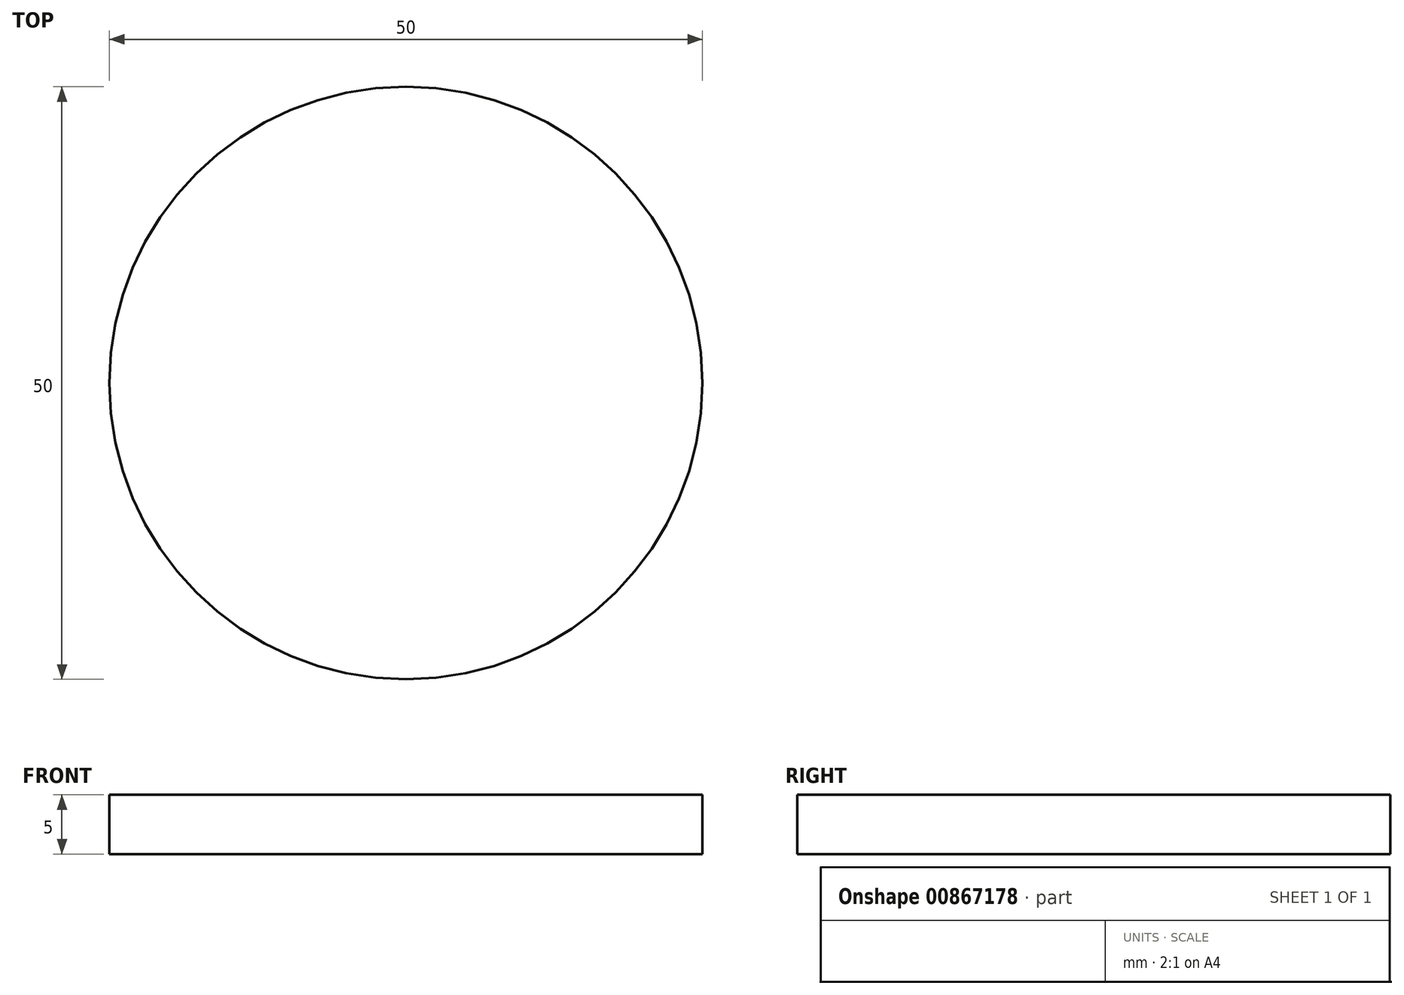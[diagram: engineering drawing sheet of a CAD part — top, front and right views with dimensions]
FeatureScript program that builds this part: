
annotation { "Feature Type Name" : "Feature", "Feature Type Description" : "" }
export const myFeature = defineFeature(function(context is Context, id is Id, definition is map)
    precondition{}
    {
        {
            var Q0;
            Q0=qCreatedBy(makeId("Top.planeOp"),FACE);
            var sketch = newSketch(context, id + "F0", { "sketchPlane" : qUnion([Q0])});
            skCircle(sketch, "E0", {"center": v(0, 0) * mm, "radius": 25 * mm});
            skSolve(sketch);
        }
        {
            var Q0;
            Q0 = qSketchRegion(id + "F0", true);
            extrude(context, id + "F1", {"entities" : qUnion([Q0]), "depth" : 5 * mm, "offsetDistance" : 25 * mm});
        }
    });
